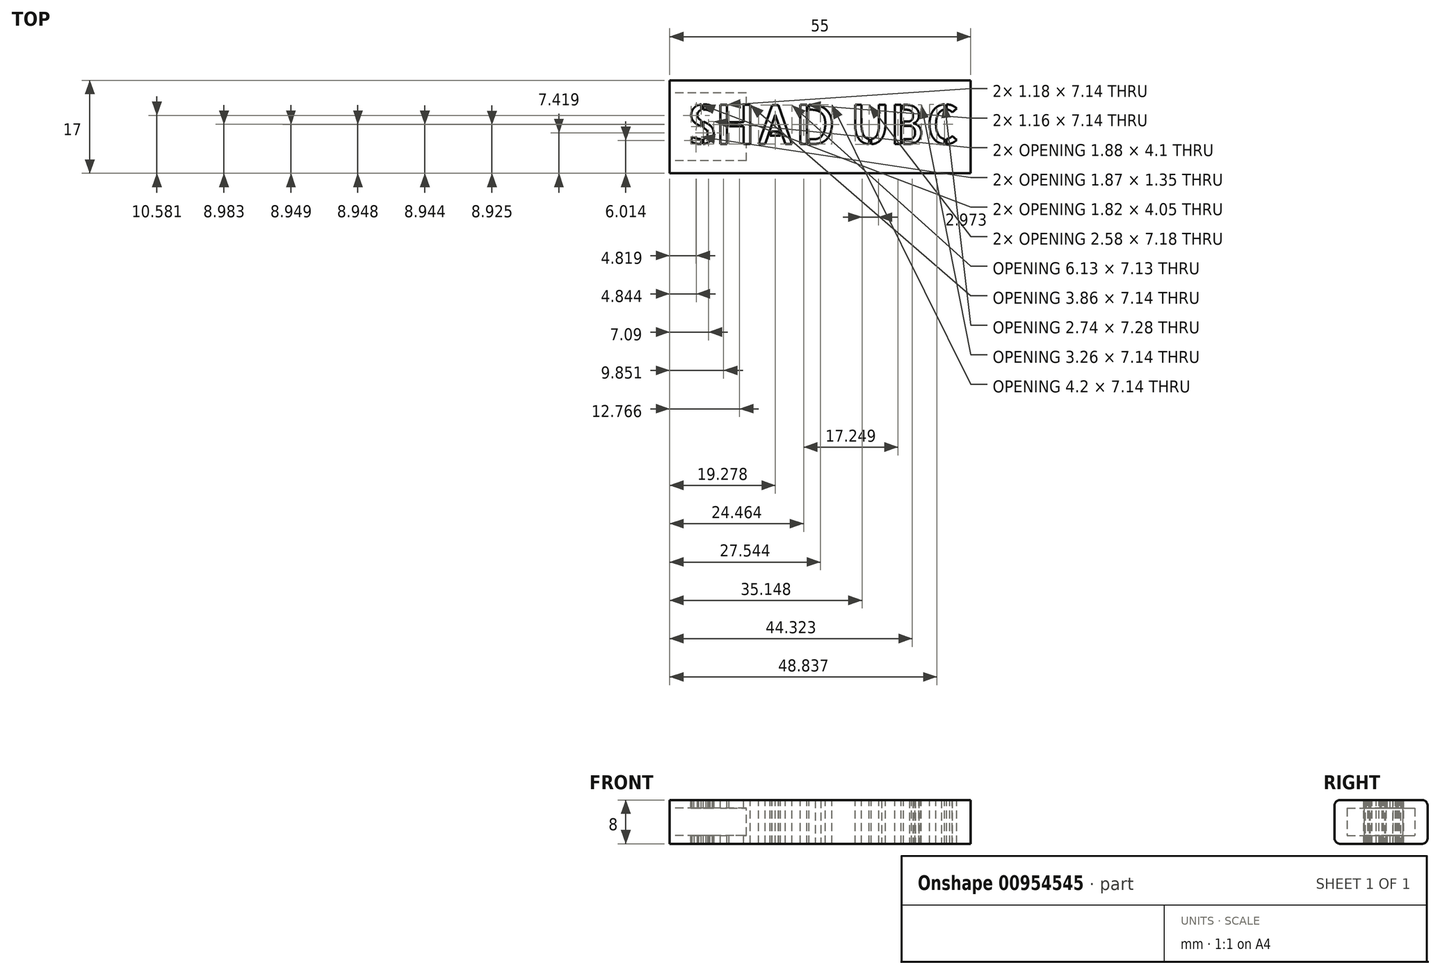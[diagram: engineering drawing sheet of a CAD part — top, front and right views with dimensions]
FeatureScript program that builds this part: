
annotation { "Feature Type Name" : "Feature", "Feature Type Description" : "" }
export const myFeature = defineFeature(function(context is Context, id is Id, definition is map)
    precondition{}
    {
        {
            var Q0;
            Q0=qCreatedBy(makeId("Front.planeOp"),FACE);
            var sketch = newSketch(context, id + "F0", { "sketchPlane" : qUnion([Q0])});
            skLineSegment(sketch, "E0.bottom", {"start": v(-7.5, 4) * mm, "end": v(7.5, 4) * mm});
            skLineSegment(sketch, "E0.top", {"start": v(-7.5, -4) * mm, "end": v(7.5, -4) * mm});
            skLineSegment(sketch, "E0.left", {"start": v(-8.5, 3) * mm, "end": v(-8.5, -3) * mm});
            skLineSegment(sketch, "E0.right", {"start": v(8.5, 3) * mm, "end": v(8.5, -3) * mm});
            skPoint(sketch, "E0.middle", {"position": v(0, 0) * mm});
            skPoint(sketch, "E1.visualSharp", {"position": v(-8.5, 4) * mm});
            skArc(sketch, "E1.filletArc", {"start": v(-7.5, 4) * mm, "mid": v(-8.2, 3.7) * mm, "end": v(-8.5, 3) * mm});
            skPoint(sketch, "E2.visualSharp", {"position": v(8.5, 4) * mm});
            skArc(sketch, "E2.filletArc", {"start": v(8.5, 3) * mm, "mid": v(8.2, 3.7) * mm, "end": v(7.5, 4) * mm});
            skPoint(sketch, "E3.visualSharp", {"position": v(8.5, -4) * mm});
            skArc(sketch, "E3.filletArc", {"start": v(7.5, -4) * mm, "mid": v(8.2, -3.7) * mm, "end": v(8.5, -3) * mm});
            skPoint(sketch, "E4.visualSharp", {"position": v(-8.5, -4) * mm});
            skArc(sketch, "E4.filletArc", {"start": v(-8.5, -3) * mm, "mid": v(-8.2, -3.7) * mm, "end": v(-7.5, -4) * mm});
            skSolve(sketch);
        }
        {
            var Q0;
            Q0 = qSketchRegion(id + "F0", true);
            extrude(context, id + "F1", {"entities" : qUnion([Q0]), "depth" : 55 * mm, "offsetDistance" : 25 * mm});
        }
        {
            var Q0;
            Q0=makeQuery(id+"F1.opExtrude","CAP_FACE",FACE,{"disambiguationData":[OSD([sQuery(id+"F0.wireOp",EDGE,"E0.bottom"),sQuery(id+"F0.wireOp",EDGE,"E0.top"),sQuery(id+"F0.wireOp",EDGE,"E0.left"),sQuery(id+"F0.wireOp",EDGE,"E0.right"),sQuery(id+"F0.wireOp",EDGE,"E1.filletArc"),sQuery(id+"F0.wireOp",EDGE,"E2.filletArc"),sQuery(id+"F0.wireOp",EDGE,"E3.filletArc"),sQuery(id+"F0.wireOp",EDGE,"E4.filletArc")])],"isStart":false});
            var sketch = newSketch(context, id + "F2", { "sketchPlane" : qUnion([Q0])});
            skLineSegment(sketch, "E5.bottom", {"start": v(6.2, 2.5) * mm, "end": v(-6.2, 2.5) * mm});
            skLineSegment(sketch, "E5.top", {"start": v(6.2, -2.5) * mm, "end": v(-6.2, -2.5) * mm});
            skLineSegment(sketch, "E5.left", {"start": v(6.2, 2.5) * mm, "end": v(6.2, -2.5) * mm});
            skLineSegment(sketch, "E5.right", {"start": v(-6.2, 2.5) * mm, "end": v(-6.2, -2.5) * mm});
            skPoint(sketch, "E5.middle", {"position": v(0, 0) * mm});
            skSolve(sketch);
        }
        {
            var Q0;
            Q0 = qSketchRegion(id + "F2", true);
            extrude(context, id + "F3", {"entities" : qUnion([Q0]), "operationType" : NewBodyOperationType.REMOVE, "oppositeDirection" : true, "depth" : 14 * mm, "offsetDistance" : 25 * mm});
        }
        {
            var Q0;
            Q0=makeQuery(id+"F1.opExtrude","SWEPT_BODY",BODY,{"disambiguationData":[OSD([sQuery(id+"F0.wireOp",EDGE,"E0.bottom"),sQuery(id+"F0.wireOp",EDGE,"E0.top"),sQuery(id+"F0.wireOp",EDGE,"E0.left"),sQuery(id+"F0.wireOp",EDGE,"E0.right"),sQuery(id+"F0.wireOp",EDGE,"E1.filletArc"),sQuery(id+"F0.wireOp",EDGE,"E2.filletArc"),sQuery(id+"F0.wireOp",EDGE,"E3.filletArc"),sQuery(id+"F0.wireOp",EDGE,"E4.filletArc")])]});
            var Q1;
            Q1=makeQuery(id+"F1.opExtrude","CAP_EDGE",EDGE,{"disambiguationData":[OSD([sQuery(id+"F0.wireOp",EDGE,"E0.right")])],"isStart":false});
            transform(context, id + "F4", {"entities" : qUnion([Q0]), "transformType" : TransformType.ROTATION, "transformAxis" : qUnion([Q1]), "angle" : 90 * degree, "makeCopy" : false});
        }
        {
            var Q0;
            Q0=makeQuery(id+"F1.opExtrude","SWEPT_FACE",FACE,{"disambiguationData":[OSD([sQuery(id+"F0.wireOp",EDGE,"E0.bottom")])]});
            var sketch = newSketch(context, id + "F5", { "sketchPlane" : qUnion([Q0])});
            skText(sketch, "E6", { "text": "SHAD UBC ", "fontName": "AllertaStencil-Regular.ttf"});
            const initialGuessF5  = {"E6": [0.0116, -0.04962, 1, 0, 0.00714]};
            skSetInitialGuess(sketch, initialGuessF5);
            skSolve(sketch);
        }
        {
            var Q0;
            Q0 = qSketchRegion(id + "F5", true);
            extrude(context, id + "F6", {"entities" : qUnion([Q0]), "operationType" : NewBodyOperationType.REMOVE, "oppositeDirection" : true, "depth" : 10 * mm, "offsetDistance" : 25 * mm});
        }
    });
